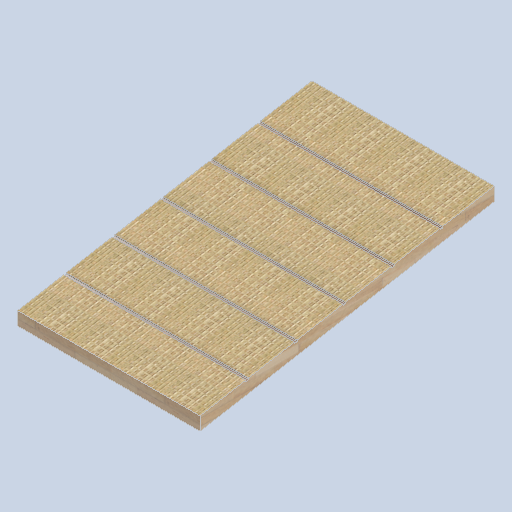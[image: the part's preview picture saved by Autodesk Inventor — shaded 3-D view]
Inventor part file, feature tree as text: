
AUTODESK INVENTOR PART (.ipt)
format: ipt  version: 2024.2 (Build 282272000, 272)  size: 503,296 bytes
history: native  units: mm
features: sketch x5, plane x3, loft x1, extrude x1, projected_geometry x1
ambient origin geometry x8: Origin, YZ Plane, XZ Plane, XY Plane, X Axis, Y Axis, Z Axis, Center Point
bodies: Solid1 (feature_tree)
feature tree (11):
  plane  "Work Plane2"
  sketch  "Sketch1"  dims[d0=0.0mm d1=2209.0mm d2=1369.0mm]
  sketch  "Sketch2"  dims[d3=100.0mm d4=17.453293mm]
  plane  "Work Plane3"
  sketch  "Sketch3"  dims[d5=100.0mm]
  loft  "Loft1"
  extrude  "Extrusion1"  Depth=100.0mm
  plane  "Work Plane1"
  sketch  "Sketch4"  dims[d6=0.0mm d7=90.0deg]
  sketch  "Sketch5"  dims[d8=0.0mm d9=90.0deg d10=350.0mm d11=10.0mm d12=20.0mm d13=350.0mm d14=20.0mm d15=350.0mm d16=350.0mm d17=350.0mm d18=0.0mm d19=0.0mm]
  projected_geometry  "Projected Loop1"
